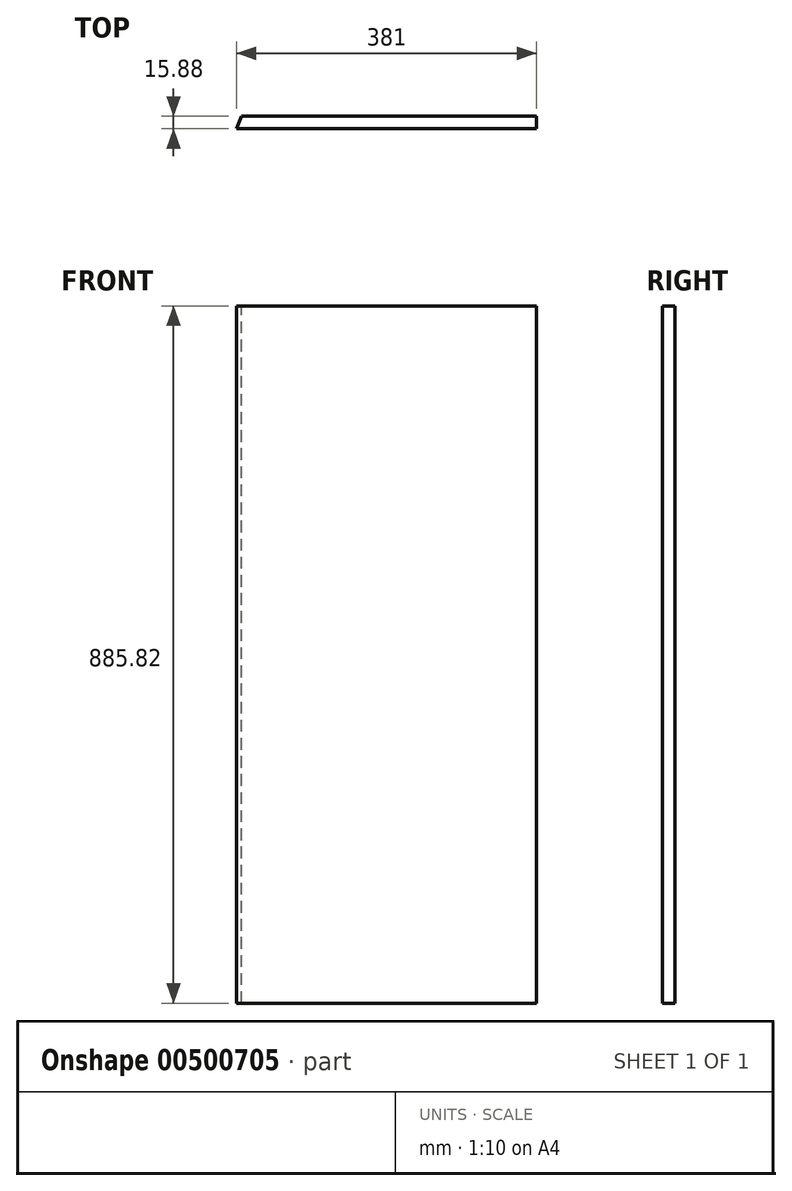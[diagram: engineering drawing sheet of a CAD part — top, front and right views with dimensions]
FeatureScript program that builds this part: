
annotation { "Feature Type Name" : "Feature", "Feature Type Description" : "" }
export const myFeature = defineFeature(function(context is Context, id is Id, definition is map)
    precondition{}
    {
        {
            var Q0;
            Q0=qCreatedBy(makeId("Front.planeOp"),FACE);
            var sketch = newSketch(context, id + "F0", { "sketchPlane" : qUnion([Q0])});
            skLineSegment(sketch, "E0.bottom", {"start": v(0, 0) * mm, "end": v(381, 0) * mm});
            skLineSegment(sketch, "E0.top", {"start": v(0, 885.83) * mm, "end": v(381, 885.83) * mm});
            skLineSegment(sketch, "E0.left", {"start": v(0, 0) * mm, "end": v(0, 885.83) * mm});
            skLineSegment(sketch, "E0.right", {"start": v(381, 0) * mm, "end": v(381, 885.83) * mm});
            skSolve(sketch);
        }
        {
            var Q0;
            Q0=makeQuery(id+"F0.imprint","IMPRINT",FACE,{"disambiguationData":[TD([[makeQuery(id+"F0.imprint","IMPRINT",EDGE,{"derivedFrom":sQuery(id+"F0.wireOp",EDGE,"E0.bottom")}),1.0]])]});
            extrude(context, id + "F1", {"entities" : qUnion([Q0]), "oppositeDirection" : true, "depth" : 15.88 * mm, "offsetDistance" : 25.4 * mm});
        }
        {
            var Q0;
            Q0=makeQuery(id+"F1.opExtrude","CAP_EDGE",EDGE,{"disambiguationData":[OSD([sQuery(id+"F0.wireOp",EDGE,"E0.left")])],"isStart":false});
            chamfer(context, id + "F2", {"entities" : qUnion([Q0]), "chamferType" : ChamferType.OFFSET_ANGLE, "width" : 15.88 * mm, "oppositeDirection" : true, "angle" : 22.5 * degree, "tangentPropagation" : true});
        }
    });
